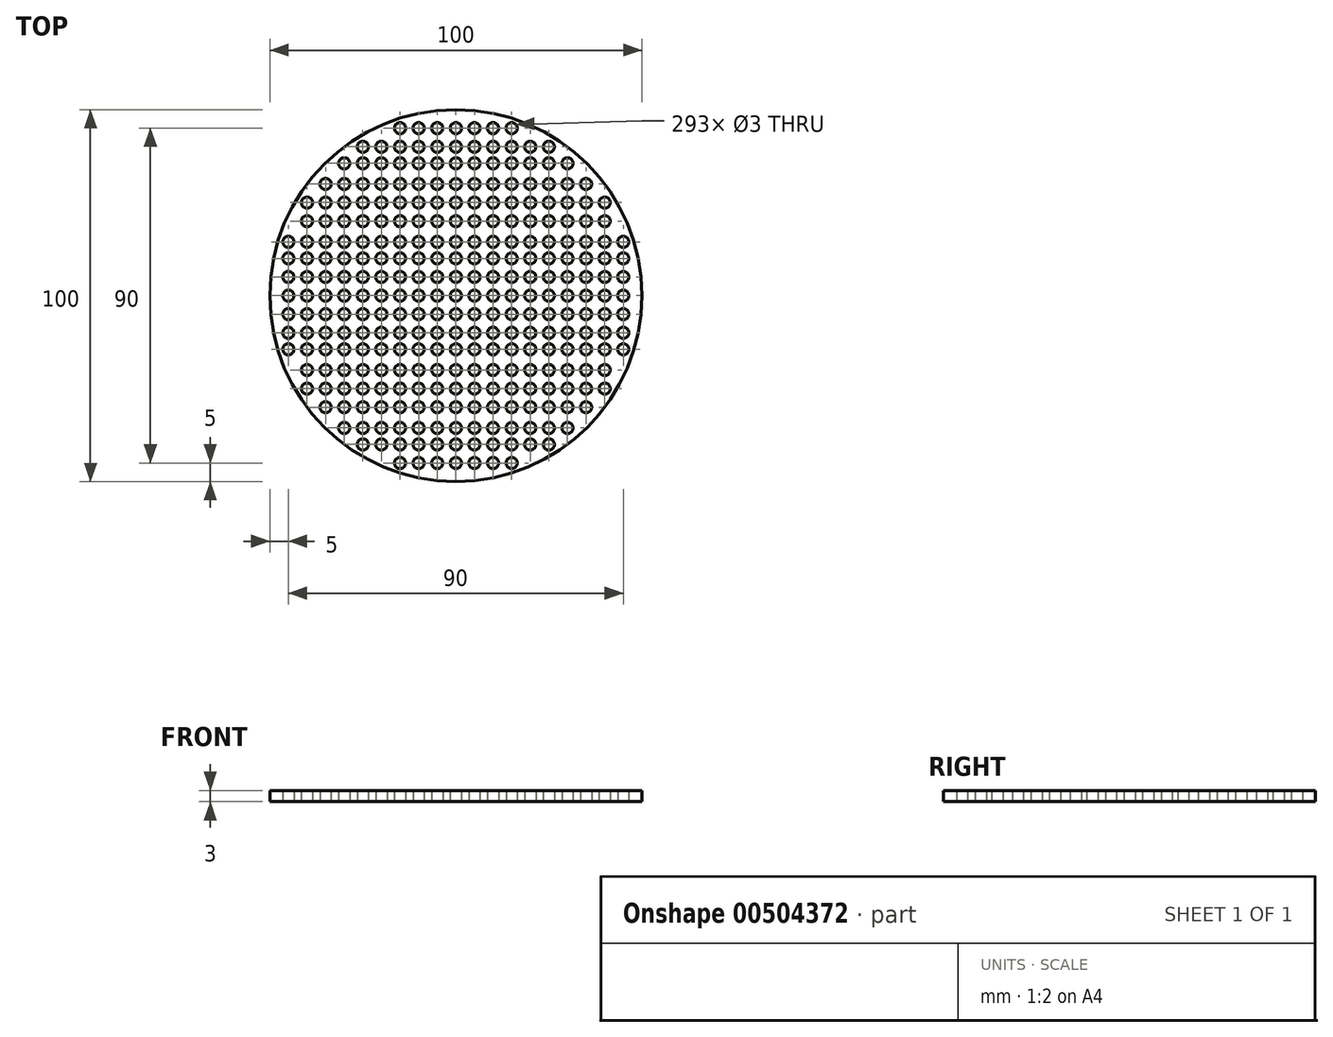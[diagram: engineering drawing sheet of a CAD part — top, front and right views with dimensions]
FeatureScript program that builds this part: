
annotation { "Feature Type Name" : "Feature", "Feature Type Description" : "" }
export const myFeature = defineFeature(function(context is Context, id is Id, definition is map)
    precondition{}
    {
        {
            var Q0;
            Q0=qCreatedBy(makeId("Top.planeOp"),FACE);
            var sketch = newSketch(context, id + "F0", { "sketchPlane" : qUnion([Q0])});
            skLineSegment(sketch, "E0.bottom", {"start": v(0, 0) * mm, "end": v(0, 0) * mm});
            skLineSegment(sketch, "E0.top", {"start": v(0, 0) * mm, "end": v(0, 0) * mm});
            skLineSegment(sketch, "E0.left", {"start": v(0, 0) * mm, "end": v(0, 0) * mm});
            skLineSegment(sketch, "E0.right", {"start": v(0, 0) * mm, "end": v(0, 0) * mm});
            skPoint(sketch, "E0.middle", {"position": v(0, 0) * mm});
            skLineSegment(sketch, "E1.bottom", {"start": v(-5, 5) * mm, "end": v(5, 5) * mm, "construction": true});
            skLineSegment(sketch, "E1.left", {"start": v(-5, 5) * mm, "end": v(-5, -5) * mm, "construction": true});
            skLineSegment(sketch, "E2.bottom", {"start": v(-10, 10) * mm, "end": v(10, 10) * mm, "construction": true});
            skLineSegment(sketch, "E2.left", {"start": v(-10, 10) * mm, "end": v(-10, -10) * mm, "construction": true});
            skLineSegment(sketch, "E2.right", {"start": v(10, 10) * mm, "end": v(10, -10) * mm, "construction": true});
            skLineSegment(sketch, "E3.bottom", {"start": v(15, 14.43) * mm, "end": v(-15, 14.43) * mm, "construction": true});
            skLineSegment(sketch, "E3.left", {"start": v(15, 14.43) * mm, "end": v(15, -14.43) * mm, "construction": true});
            skLineSegment(sketch, "E3.right", {"start": v(-15, 14.43) * mm, "end": v(-15, -14.43) * mm, "construction": true});
            skLineSegment(sketch, "E4.bottom", {"start": v(20, 20) * mm, "end": v(-20, 20) * mm, "construction": true});
            skLineSegment(sketch, "E4.left", {"start": v(20, 20) * mm, "end": v(20, -20) * mm, "construction": true});
            skLineSegment(sketch, "E4.right", {"start": v(-20, 20) * mm, "end": v(-20, -20) * mm, "construction": true});
            skLineSegment(sketch, "E5.bottom", {"start": v(25, 25) * mm, "end": v(-25, 25) * mm, "construction": true});
            skLineSegment(sketch, "E5.left", {"start": v(25, 25) * mm, "end": v(25, -25) * mm, "construction": true});
            skLineSegment(sketch, "E5.right", {"start": v(-25, 25) * mm, "end": v(-25, -25) * mm, "construction": true});
            skCircle(sketch, "E6", {"center": v(0, 0) * mm, "radius": 1.5 * mm});
            skCircle(sketch, "E7", {"center": v(-5, 5) * mm, "radius": 1.5 * mm});
            skCircle(sketch, "E8", {"center": v(-10, 10) * mm, "radius": 1.5 * mm});
            skCircle(sketch, "E9", {"center": v(-15, 14.43) * mm, "radius": 1.5 * mm});
            skCircle(sketch, "E10", {"center": v(-20, 20) * mm, "radius": 1.5 * mm});
            skCircle(sketch, "E11", {"center": v(-25, 25) * mm, "radius": 1.5 * mm});
            skCircle(sketch, "E12", {"center": v(-5, 10) * mm, "radius": 1.5 * mm});
            skCircle(sketch, "E13", {"center": v(-5, 14.43) * mm, "radius": 1.5 * mm});
            skCircle(sketch, "E14", {"center": v(-5, 20) * mm, "radius": 1.5 * mm});
            skCircle(sketch, "E15", {"center": v(-5, 25) * mm, "radius": 1.5 * mm});
            skCircle(sketch, "E16", {"center": v(-10, 14.43) * mm, "radius": 1.5 * mm});
            skCircle(sketch, "E17", {"center": v(-10, 20) * mm, "radius": 1.5 * mm});
            skCircle(sketch, "E18", {"center": v(-10, 25) * mm, "radius": 1.5 * mm});
            skCircle(sketch, "E19", {"center": v(-15, 20) * mm, "radius": 1.5 * mm});
            skCircle(sketch, "E20", {"center": v(-15, 25) * mm, "radius": 1.5 * mm});
            skCircle(sketch, "E21", {"center": v(-20, 25) * mm, "radius": 1.5 * mm});
            skCircle(sketch, "E22", {"center": v(-10, 5) * mm, "radius": 1.5 * mm});
            skCircle(sketch, "E23", {"center": v(-15, 5) * mm, "radius": 1.5 * mm});
            skCircle(sketch, "E24", {"center": v(-20, 5) * mm, "radius": 1.5 * mm});
            skCircle(sketch, "E25", {"center": v(-25, 5) * mm, "radius": 1.5 * mm});
            skCircle(sketch, "E26", {"center": v(-15, 10) * mm, "radius": 1.5 * mm});
            skCircle(sketch, "E27", {"center": v(-20, 10) * mm, "radius": 1.5 * mm});
            skCircle(sketch, "E28", {"center": v(-25, 10) * mm, "radius": 1.5 * mm});
            skCircle(sketch, "E29", {"center": v(-20, 14.43) * mm, "radius": 1.5 * mm});
            skCircle(sketch, "E30", {"center": v(-25, 14.43) * mm, "radius": 1.5 * mm});
            skCircle(sketch, "E31", {"center": v(-25, 20) * mm, "radius": 1.5 * mm});
            skCircle(sketch, "E32", {"center": v(-5, 0) * mm, "radius": 1.5 * mm});
            skCircle(sketch, "E33", {"center": v(-10, 0) * mm, "radius": 1.5 * mm});
            skCircle(sketch, "E34", {"center": v(-15, 0) * mm, "radius": 1.5 * mm});
            skCircle(sketch, "E35", {"center": v(-20, 0) * mm, "radius": 1.5 * mm});
            skCircle(sketch, "E36", {"center": v(-25, 0) * mm, "radius": 1.5 * mm});
            skCircle(sketch, "E37", {"center": v(0, 5) * mm, "radius": 1.5 * mm});
            skCircle(sketch, "E38", {"center": v(0, 10) * mm, "radius": 1.5 * mm});
            skCircle(sketch, "E39", {"center": v(0, 14.43) * mm, "radius": 1.5 * mm});
            skCircle(sketch, "E40", {"center": v(0, 20) * mm, "radius": 1.5 * mm});
            skCircle(sketch, "E41", {"center": v(0, 25) * mm, "radius": 1.5 * mm});
            skCircle(sketch, "E42", {"center": v(0, 0) * mm, "radius": 50 * mm});
            skCircle(sketch, "E43.MirrorC", {"center": v(-15, 30) * mm, "radius": 1.5 * mm});
            skLineSegment(sketch, "E44.MirrorCS", {"start": v(20, 30) * mm, "end": v(-20, 30) * mm, "construction": true});
            skLineSegment(sketch, "E45.MirrorCS", {"start": v(15, 35.57) * mm, "end": v(-15, 35.57) * mm, "construction": true});
            skLineSegment(sketch, "E46.MirrorCS", {"start": v(-10, 40) * mm, "end": v(10, 40) * mm, "construction": true});
            skLineSegment(sketch, "E47.MirrorCS", {"start": v(-5, 45) * mm, "end": v(5, 45) * mm, "construction": true});
            skCircle(sketch, "E48.MirrorC", {"center": v(-10, 30) * mm, "radius": 1.5 * mm});
            skCircle(sketch, "E49.MirrorC", {"center": v(-10, 35.57) * mm, "radius": 1.5 * mm});
            skCircle(sketch, "E50.MirrorC", {"center": v(-5, 30) * mm, "radius": 1.5 * mm});
            skCircle(sketch, "E51.MirrorC", {"center": v(-25, 35.57) * mm, "radius": 1.5 * mm});
            skCircle(sketch, "E52.MirrorC", {"center": v(-20, 40) * mm, "radius": 1.5 * mm});
            skCircle(sketch, "E53.MirrorC", {"center": v(0, 45) * mm, "radius": 1.5 * mm});
            skCircle(sketch, "E54.MirrorC", {"center": v(-25, 40) * mm, "radius": 1.5 * mm});
            skCircle(sketch, "E55.MirrorC", {"center": v(-5, 40) * mm, "radius": 1.5 * mm});
            skCircle(sketch, "E56.MirrorC", {"center": v(0, 40) * mm, "radius": 1.5 * mm});
            skCircle(sketch, "E57.MirrorC", {"center": v(-10, 45) * mm, "radius": 1.5 * mm});
            skCircle(sketch, "E58.MirrorC", {"center": v(-25, 30) * mm, "radius": 1.5 * mm});
            skCircle(sketch, "E59.MirrorC", {"center": v(-15, 40) * mm, "radius": 1.5 * mm});
            skCircle(sketch, "E60.MirrorC", {"center": v(-20, 35.57) * mm, "radius": 1.5 * mm});
            skCircle(sketch, "E61.MirrorC", {"center": v(-5, 45) * mm, "radius": 1.5 * mm});
            skCircle(sketch, "E62.MirrorC", {"center": v(-20, 30) * mm, "radius": 1.5 * mm});
            skCircle(sketch, "E63.MirrorC", {"center": v(0, 30) * mm, "radius": 1.5 * mm});
            skCircle(sketch, "E64.MirrorC", {"center": v(-10, 40) * mm, "radius": 1.5 * mm});
            skCircle(sketch, "E65.MirrorC", {"center": v(-15, 45) * mm, "radius": 1.5 * mm});
            skCircle(sketch, "E66.MirrorC", {"center": v(-15, 35.57) * mm, "radius": 1.5 * mm});
            skCircle(sketch, "E67.MirrorC", {"center": v(-5, 35.57) * mm, "radius": 1.5 * mm});
            skCircle(sketch, "E68.MirrorC", {"center": v(0, 35.57) * mm, "radius": 1.5 * mm});
            skCircle(sketch, "E69.MirrorC", {"center": v(-35, 25) * mm, "radius": 1.5 * mm});
            skCircle(sketch, "E70.MirrorC", {"center": v(-35, 20) * mm, "radius": 1.5 * mm});
            skCircle(sketch, "E71.MirrorC", {"center": v(-40, 25) * mm, "radius": 1.5 * mm});
            skCircle(sketch, "E72.MirrorC", {"center": v(-30, 25) * mm, "radius": 1.5 * mm});
            skCircle(sketch, "E73.MirrorC", {"center": v(-40, 5) * mm, "radius": 1.5 * mm});
            skCircle(sketch, "E74.MirrorC", {"center": v(-35, 30) * mm, "radius": 1.5 * mm});
            skCircle(sketch, "E75.MirrorC", {"center": v(-45, 5) * mm, "radius": 1.5 * mm});
            skCircle(sketch, "E76.MirrorC", {"center": v(-35, 5) * mm, "radius": 1.5 * mm});
            skCircle(sketch, "E77.MirrorC", {"center": v(-40, 10) * mm, "radius": 1.5 * mm});
            skCircle(sketch, "E78.MirrorC", {"center": v(-30, 5) * mm, "radius": 1.5 * mm});
            skCircle(sketch, "E79.MirrorC", {"center": v(-30, 35.57) * mm, "radius": 1.5 * mm});
            skCircle(sketch, "E80.MirrorC", {"center": v(-35, 14.43) * mm, "radius": 1.5 * mm});
            skCircle(sketch, "E81.MirrorC", {"center": v(-45, 10) * mm, "radius": 1.5 * mm});
            skCircle(sketch, "E82.MirrorC", {"center": v(-40, 20) * mm, "radius": 1.5 * mm});
            skCircle(sketch, "E83.MirrorC", {"center": v(-30, 20) * mm, "radius": 1.5 * mm});
            skCircle(sketch, "E84.MirrorC", {"center": v(-45, 14.43) * mm, "radius": 1.5 * mm});
            skCircle(sketch, "E85.MirrorC", {"center": v(-30, 14.43) * mm, "radius": 1.5 * mm});
            skCircle(sketch, "E86.MirrorC", {"center": v(-30, 10) * mm, "radius": 1.5 * mm});
            skCircle(sketch, "E87.MirrorC", {"center": v(-40, 14.43) * mm, "radius": 1.5 * mm});
            skCircle(sketch, "E88.MirrorC", {"center": v(-30, 30) * mm, "radius": 1.5 * mm});
            skCircle(sketch, "E89.MirrorC", {"center": v(-35, 10) * mm, "radius": 1.5 * mm});
            skCircle(sketch, "E90.MirrorC", {"center": v(-40, 0) * mm, "radius": 1.5 * mm});
            skCircle(sketch, "E91.MirrorC", {"center": v(-45, 0) * mm, "radius": 1.5 * mm});
            skCircle(sketch, "E92.MirrorC", {"center": v(-35, 0) * mm, "radius": 1.5 * mm});
            skCircle(sketch, "E93.MirrorC", {"center": v(-30, 0) * mm, "radius": 1.5 * mm});
            skLineSegment(sketch, "E94.MirrorCS", {"start": v(5, 5) * mm, "end": v(-5, 5) * mm, "construction": true});
            skCircle(sketch, "E95.MirrorC", {"center": v(5, 5) * mm, "radius": 1.5 * mm});
            skCircle(sketch, "E96.MirrorC", {"center": v(40, 5) * mm, "radius": 1.5 * mm});
            skCircle(sketch, "E97.MirrorC", {"center": v(10, 10) * mm, "radius": 1.5 * mm});
            skCircle(sketch, "E98.MirrorC", {"center": v(35, 5) * mm, "radius": 1.5 * mm});
            skCircle(sketch, "E99.MirrorC", {"center": v(25, 25) * mm, "radius": 1.5 * mm});
            skCircle(sketch, "E100.MirrorC", {"center": v(10, 40) * mm, "radius": 1.5 * mm});
            skCircle(sketch, "E101.MirrorC", {"center": v(5, 45) * mm, "radius": 1.5 * mm});
            skCircle(sketch, "E102.MirrorC", {"center": v(20, 30) * mm, "radius": 1.5 * mm});
            skLineSegment(sketch, "E103.MirrorCS", {"start": v(5, 45) * mm, "end": v(-5, 45) * mm, "construction": true});
            skCircle(sketch, "E104.MirrorC", {"center": v(25, 35.57) * mm, "radius": 1.5 * mm});
            skCircle(sketch, "E105.MirrorC", {"center": v(5, 40) * mm, "radius": 1.5 * mm});
            skCircle(sketch, "E106.MirrorC", {"center": v(25, 10) * mm, "radius": 1.5 * mm});
            skCircle(sketch, "E107.MirrorC", {"center": v(5, 35.57) * mm, "radius": 1.5 * mm});
            skCircle(sketch, "E108.MirrorC", {"center": v(35, 30) * mm, "radius": 1.5 * mm});
            skCircle(sketch, "E109.MirrorC", {"center": v(25, 30) * mm, "radius": 1.5 * mm});
            skCircle(sketch, "E110.MirrorC", {"center": v(5, 25) * mm, "radius": 1.5 * mm});
            skCircle(sketch, "E111.MirrorC", {"center": v(45, 5) * mm, "radius": 1.5 * mm});
            skCircle(sketch, "E112.MirrorC", {"center": v(20, 40) * mm, "radius": 1.5 * mm});
            skCircle(sketch, "E113.MirrorC", {"center": v(25, 40) * mm, "radius": 1.5 * mm});
            skCircle(sketch, "E114.MirrorC", {"center": v(10, 5) * mm, "radius": 1.5 * mm});
            skCircle(sketch, "E115.MirrorC", {"center": v(30, 5) * mm, "radius": 1.5 * mm});
            skCircle(sketch, "E116.MirrorC", {"center": v(35, 0) * mm, "radius": 1.5 * mm});
            skCircle(sketch, "E117.MirrorC", {"center": v(5, 30) * mm, "radius": 1.5 * mm});
            skCircle(sketch, "E118.MirrorC", {"center": v(35, 10) * mm, "radius": 1.5 * mm});
            skCircle(sketch, "E119.MirrorC", {"center": v(40, 25) * mm, "radius": 1.5 * mm});
            skCircle(sketch, "E120.MirrorC", {"center": v(10, 25) * mm, "radius": 1.5 * mm});
            skCircle(sketch, "E121.MirrorC", {"center": v(20, 10) * mm, "radius": 1.5 * mm});
            skCircle(sketch, "E122.MirrorC", {"center": v(40, 10) * mm, "radius": 1.5 * mm});
            skCircle(sketch, "E123.MirrorC", {"center": v(20, 35.57) * mm, "radius": 1.5 * mm});
            skCircle(sketch, "E124.MirrorC", {"center": v(5, 10) * mm, "radius": 1.5 * mm});
            skCircle(sketch, "E125.MirrorC", {"center": v(20, 5) * mm, "radius": 1.5 * mm});
            skCircle(sketch, "E126.MirrorC", {"center": v(10, 30) * mm, "radius": 1.5 * mm});
            skCircle(sketch, "E127.MirrorC", {"center": v(25, 5) * mm, "radius": 1.5 * mm});
            skCircle(sketch, "E128.MirrorC", {"center": v(10, 35.57) * mm, "radius": 1.5 * mm});
            skCircle(sketch, "E129.MirrorC", {"center": v(20, 25) * mm, "radius": 1.5 * mm});
            skCircle(sketch, "E130.MirrorC", {"center": v(10, 45) * mm, "radius": 1.5 * mm});
            skCircle(sketch, "E131.MirrorC", {"center": v(35, 25) * mm, "radius": 1.5 * mm});
            skCircle(sketch, "E132.MirrorC", {"center": v(15, 30) * mm, "radius": 1.5 * mm});
            skCircle(sketch, "E133.MirrorC", {"center": v(30, 20) * mm, "radius": 1.5 * mm});
            skCircle(sketch, "E134.MirrorC", {"center": v(40, 20) * mm, "radius": 1.5 * mm});
            skLineSegment(sketch, "E135.MirrorCS", {"start": v(10, 40) * mm, "end": v(-10, 40) * mm, "construction": true});
            skLineSegment(sketch, "E136.MirrorCS", {"start": v(5, 5) * mm, "end": v(5, -5) * mm, "construction": true});
            skLineSegment(sketch, "E137.MirrorCS", {"start": v(-15, 14.43) * mm, "end": v(15, 14.43) * mm, "construction": true});
            skLineSegment(sketch, "E138.MirrorCS", {"start": v(-20, 20) * mm, "end": v(20, 20) * mm, "construction": true});
            skLineSegment(sketch, "E139.MirrorCS", {"start": v(-25, 25) * mm, "end": v(25, 25) * mm, "construction": true});
            skCircle(sketch, "E140.MirrorC", {"center": v(15, 20) * mm, "radius": 1.5 * mm});
            skCircle(sketch, "E141.MirrorC", {"center": v(20, 0) * mm, "radius": 1.5 * mm});
            skCircle(sketch, "E142.MirrorC", {"center": v(30, 10) * mm, "radius": 1.5 * mm});
            skLineSegment(sketch, "E143.MirrorCS", {"start": v(-15, 35.57) * mm, "end": v(15, 35.57) * mm, "construction": true});
            skCircle(sketch, "E144.MirrorC", {"center": v(20, 14.43) * mm, "radius": 1.5 * mm});
            skLineSegment(sketch, "E145.MirrorCS", {"start": v(-20, 30) * mm, "end": v(20, 30) * mm, "construction": true});
            skCircle(sketch, "E146.MirrorC", {"center": v(15, 5) * mm, "radius": 1.5 * mm});
            skCircle(sketch, "E147.MirrorC", {"center": v(30, 30) * mm, "radius": 1.5 * mm});
            skCircle(sketch, "E148.MirrorC", {"center": v(45, 0) * mm, "radius": 1.5 * mm});
            skCircle(sketch, "E149.MirrorC", {"center": v(45, 14.43) * mm, "radius": 1.5 * mm});
            skCircle(sketch, "E150.MirrorC", {"center": v(15, 25) * mm, "radius": 1.5 * mm});
            skCircle(sketch, "E151.MirrorC", {"center": v(5, 14.43) * mm, "radius": 1.5 * mm});
            skCircle(sketch, "E152.MirrorC", {"center": v(35, 20) * mm, "radius": 1.5 * mm});
            skCircle(sketch, "E153.MirrorC", {"center": v(30, 25) * mm, "radius": 1.5 * mm});
            skCircle(sketch, "E154.MirrorC", {"center": v(10, 14.43) * mm, "radius": 1.5 * mm});
            skCircle(sketch, "E155.MirrorC", {"center": v(35, 14.43) * mm, "radius": 1.5 * mm});
            skCircle(sketch, "E156.MirrorC", {"center": v(5, 20) * mm, "radius": 1.5 * mm});
            skCircle(sketch, "E157.MirrorC", {"center": v(25, 14.43) * mm, "radius": 1.5 * mm});
            skCircle(sketch, "E158.MirrorC", {"center": v(10, 0) * mm, "radius": 1.5 * mm});
            skLineSegment(sketch, "E159.MirrorCS", {"start": v(10, 10) * mm, "end": v(-10, 10) * mm, "construction": true});
            skCircle(sketch, "E160.MirrorC", {"center": v(10, 20) * mm, "radius": 1.5 * mm});
            skCircle(sketch, "E161.MirrorC", {"center": v(15, 35.57) * mm, "radius": 1.5 * mm});
            skCircle(sketch, "E162.MirrorC", {"center": v(15, 10) * mm, "radius": 1.5 * mm});
            skCircle(sketch, "E163.MirrorC", {"center": v(15, 45) * mm, "radius": 1.5 * mm});
            skCircle(sketch, "E164.MirrorC", {"center": v(20, 20) * mm, "radius": 1.5 * mm});
            skCircle(sketch, "E165.MirrorC", {"center": v(30, 0) * mm, "radius": 1.5 * mm});
            skCircle(sketch, "E166.MirrorC", {"center": v(15, 0) * mm, "radius": 1.5 * mm});
            skCircle(sketch, "E167.MirrorC", {"center": v(30, 35.57) * mm, "radius": 1.5 * mm});
            skCircle(sketch, "E168.MirrorC", {"center": v(15, 40) * mm, "radius": 1.5 * mm});
            skCircle(sketch, "E169.MirrorC", {"center": v(40, 14.43) * mm, "radius": 1.5 * mm});
            skCircle(sketch, "E170.MirrorC", {"center": v(40, 0) * mm, "radius": 1.5 * mm});
            skCircle(sketch, "E171.MirrorC", {"center": v(25, 0) * mm, "radius": 1.5 * mm});
            skCircle(sketch, "E172.MirrorC", {"center": v(45, 10) * mm, "radius": 1.5 * mm});
            skCircle(sketch, "E173.MirrorC", {"center": v(30, 14.43) * mm, "radius": 1.5 * mm});
            skCircle(sketch, "E174.MirrorC", {"center": v(15, 14.43) * mm, "radius": 1.5 * mm});
            skCircle(sketch, "E175.MirrorC", {"center": v(5, 0) * mm, "radius": 1.5 * mm});
            skCircle(sketch, "E176.MirrorC", {"center": v(25, 20) * mm, "radius": 1.5 * mm});
            skCircle(sketch, "E177.MirrorC", {"center": v(20, -20) * mm, "radius": 1.5 * mm});
            skCircle(sketch, "E178.MirrorC", {"center": v(25, -25) * mm, "radius": 1.5 * mm});
            skCircle(sketch, "E179.MirrorC", {"center": v(-25, -25) * mm, "radius": 1.5 * mm});
            skCircle(sketch, "E180.MirrorC", {"center": v(5, -5) * mm, "radius": 1.5 * mm});
            skCircle(sketch, "E181.MirrorC", {"center": v(-10, -10) * mm, "radius": 1.5 * mm});
            skCircle(sketch, "E182.MirrorC", {"center": v(-30, -5) * mm, "radius": 1.5 * mm});
            skCircle(sketch, "E183.MirrorC", {"center": v(20, -30) * mm, "radius": 1.5 * mm});
            skCircle(sketch, "E184.MirrorC", {"center": v(35, -5) * mm, "radius": 1.5 * mm});
            skCircle(sketch, "E185.MirrorC", {"center": v(-10, -40) * mm, "radius": 1.5 * mm});
            skCircle(sketch, "E186.MirrorC", {"center": v(5, -45) * mm, "radius": 1.5 * mm});
            skCircle(sketch, "E187.MirrorC", {"center": v(-40, -5) * mm, "radius": 1.5 * mm});
            skCircle(sketch, "E188.MirrorC", {"center": v(-45, -5) * mm, "radius": 1.5 * mm});
            skLineSegment(sketch, "E189.MirrorCS", {"start": v(5, -45) * mm, "end": v(-5, -45) * mm, "construction": true});
            skCircle(sketch, "E190.MirrorC", {"center": v(40, -25) * mm, "radius": 1.5 * mm});
            skCircle(sketch, "E191.MirrorC", {"center": v(-40, -10) * mm, "radius": 1.5 * mm});
            skCircle(sketch, "E192.MirrorC", {"center": v(15, -10) * mm, "radius": 1.5 * mm});
            skCircle(sketch, "E193.MirrorC", {"center": v(40, -5) * mm, "radius": 1.5 * mm});
            skCircle(sketch, "E194.MirrorC", {"center": v(35, -10) * mm, "radius": 1.5 * mm});
            skCircle(sketch, "E195.MirrorC", {"center": v(-25, -10) * mm, "radius": 1.5 * mm});
            skCircle(sketch, "E196.MirrorC", {"center": v(-35, -5) * mm, "radius": 1.5 * mm});
            skCircle(sketch, "E197.MirrorC", {"center": v(5, -30) * mm, "radius": 1.5 * mm});
            skCircle(sketch, "E198.MirrorC", {"center": v(-15, -30) * mm, "radius": 1.5 * mm});
            skCircle(sketch, "E199.MirrorC", {"center": v(20, -35.57) * mm, "radius": 1.5 * mm});
            skCircle(sketch, "E200.MirrorC", {"center": v(-15, -40) * mm, "radius": 1.5 * mm});
            skCircle(sketch, "E201.MirrorC", {"center": v(35, -20) * mm, "radius": 1.5 * mm});
            skCircle(sketch, "E202.MirrorC", {"center": v(-15, -45) * mm, "radius": 1.5 * mm});
            skCircle(sketch, "E203.MirrorC", {"center": v(-45, -10) * mm, "radius": 1.5 * mm});
            skCircle(sketch, "E204.MirrorC", {"center": v(-10, -20) * mm, "radius": 1.5 * mm});
            skLineSegment(sketch, "E205.MirrorCS", {"start": v(-20, -30) * mm, "end": v(20, -30) * mm, "construction": true});
            skLineSegment(sketch, "E206.MirrorCS", {"start": v(-10, -40) * mm, "end": v(10, -40) * mm, "construction": true});
            skCircle(sketch, "E207.MirrorC", {"center": v(35, -30) * mm, "radius": 1.5 * mm});
            skCircle(sketch, "E208.MirrorC", {"center": v(30, -5) * mm, "radius": 1.5 * mm});
            skCircle(sketch, "E209.MirrorC", {"center": v(-15, -5) * mm, "radius": 1.5 * mm});
            skCircle(sketch, "E210.MirrorC", {"center": v(-15, -20) * mm, "radius": 1.5 * mm});
            skCircle(sketch, "E211.MirrorC", {"center": v(-10, -30) * mm, "radius": 1.5 * mm});
            skCircle(sketch, "E212.MirrorC", {"center": v(5, -10) * mm, "radius": 1.5 * mm});
            skCircle(sketch, "E213.MirrorC", {"center": v(20, -5) * mm, "radius": 1.5 * mm});
            skCircle(sketch, "E214.MirrorC", {"center": v(-30, -10) * mm, "radius": 1.5 * mm});
            skCircle(sketch, "E215.MirrorC", {"center": v(20, -40) * mm, "radius": 1.5 * mm});
            skCircle(sketch, "E216.MirrorC", {"center": v(-10, -5) * mm, "radius": 1.5 * mm});
            skCircle(sketch, "E217.MirrorC", {"center": v(0, -10) * mm, "radius": 1.5 * mm});
            skLineSegment(sketch, "E218.MirrorCS", {"start": v(5, -5) * mm, "end": v(-5, -5) * mm, "construction": true});
            skLineSegment(sketch, "E219.MirrorCS", {"start": v(-20, -20) * mm, "end": v(20, -20) * mm, "construction": true});
            skCircle(sketch, "E220.MirrorC", {"center": v(-10, -25) * mm, "radius": 1.5 * mm});
            skCircle(sketch, "E221.MirrorC", {"center": v(0, -40) * mm, "radius": 1.5 * mm});
            skLineSegment(sketch, "E222.MirrorCS", {"start": v(-25, -25) * mm, "end": v(25, -25) * mm, "construction": true});
            skCircle(sketch, "E223.MirrorC", {"center": v(-25, -40) * mm, "radius": 1.5 * mm});
            skCircle(sketch, "E224.MirrorC", {"center": v(-15, -10) * mm, "radius": 1.5 * mm});
            skCircle(sketch, "E225.MirrorC", {"center": v(5, -25) * mm, "radius": 1.5 * mm});
            skCircle(sketch, "E226.MirrorC", {"center": v(-30, -25) * mm, "radius": 1.5 * mm});
            skCircle(sketch, "E227.MirrorC", {"center": v(-30, -30) * mm, "radius": 1.5 * mm});
            skCircle(sketch, "E228.MirrorC", {"center": v(25, -40) * mm, "radius": 1.5 * mm});
            skLineSegment(sketch, "E229.MirrorCS", {"start": v(-15, -14.43) * mm, "end": v(15, -14.43) * mm, "construction": true});
            skCircle(sketch, "E230.MirrorC", {"center": v(40, -10) * mm, "radius": 1.5 * mm});
            skCircle(sketch, "E231.MirrorC", {"center": v(-40, -25) * mm, "radius": 1.5 * mm});
            skCircle(sketch, "E232.MirrorC", {"center": v(45, -5) * mm, "radius": 1.5 * mm});
            skCircle(sketch, "E233.MirrorC", {"center": v(-30, -20) * mm, "radius": 1.5 * mm});
            skCircle(sketch, "E234.MirrorC", {"center": v(5, -20) * mm, "radius": 1.5 * mm});
            skLineSegment(sketch, "E235.MirrorCS", {"start": v(-15, -35.57) * mm, "end": v(15, -35.57) * mm, "construction": true});
            skCircle(sketch, "E236.MirrorC", {"center": v(20, -14.43) * mm, "radius": 1.5 * mm});
            skCircle(sketch, "E237.MirrorC", {"center": v(15, -40) * mm, "radius": 1.5 * mm});
            skCircle(sketch, "E238.MirrorC", {"center": v(-15, -25) * mm, "radius": 1.5 * mm});
            skCircle(sketch, "E239.MirrorC", {"center": v(0, -25) * mm, "radius": 1.5 * mm});
            skCircle(sketch, "E240.MirrorC", {"center": v(-10, -45) * mm, "radius": 1.5 * mm});
            skCircle(sketch, "E241.MirrorC", {"center": v(35, -25) * mm, "radius": 1.5 * mm});
            skCircle(sketch, "E242.MirrorC", {"center": v(-25, -30) * mm, "radius": 1.5 * mm});
            skCircle(sketch, "E243.MirrorC", {"center": v(20, -25) * mm, "radius": 1.5 * mm});
            skLineSegment(sketch, "E244.MirrorCS", {"start": v(10, -10) * mm, "end": v(-10, -10) * mm, "construction": true});
            skCircle(sketch, "E245.MirrorC", {"center": v(20, -10) * mm, "radius": 1.5 * mm});
            skCircle(sketch, "E246.MirrorC", {"center": v(25, -10) * mm, "radius": 1.5 * mm});
            skCircle(sketch, "E247.MirrorC", {"center": v(5, -40) * mm, "radius": 1.5 * mm});
            skCircle(sketch, "E248.MirrorC", {"center": v(-25, -5) * mm, "radius": 1.5 * mm});
            skCircle(sketch, "E249.MirrorC", {"center": v(15, -25) * mm, "radius": 1.5 * mm});
            skCircle(sketch, "E250.MirrorC", {"center": v(15, -45) * mm, "radius": 1.5 * mm});
            skCircle(sketch, "E251.MirrorC", {"center": v(25, -20) * mm, "radius": 1.5 * mm});
            skCircle(sketch, "E252.MirrorC", {"center": v(-20, -14.43) * mm, "radius": 1.5 * mm});
            skLineSegment(sketch, "E253.MirrorCS", {"start": v(15, -35.57) * mm, "end": v(-15, -35.57) * mm, "construction": true});
            skCircle(sketch, "E254.MirrorC", {"center": v(-5, -45) * mm, "radius": 1.5 * mm});
            skCircle(sketch, "E255.MirrorC", {"center": v(-5, -14.43) * mm, "radius": 1.5 * mm});
            skCircle(sketch, "E256.MirrorC", {"center": v(30, -30) * mm, "radius": 1.5 * mm});
            skCircle(sketch, "E257.MirrorC", {"center": v(40, -20) * mm, "radius": 1.5 * mm});
            skLineSegment(sketch, "E258.MirrorCS", {"start": v(20, -30) * mm, "end": v(-20, -30) * mm, "construction": true});
            skCircle(sketch, "E259.MirrorC", {"center": v(-20, -35.57) * mm, "radius": 1.5 * mm});
            skCircle(sketch, "E260.MirrorC", {"center": v(-5, -10) * mm, "radius": 1.5 * mm});
            skCircle(sketch, "E261.MirrorC", {"center": v(15, -5) * mm, "radius": 1.5 * mm});
            skCircle(sketch, "E262.MirrorC", {"center": v(15, -35.57) * mm, "radius": 1.5 * mm});
            skCircle(sketch, "E263.MirrorC", {"center": v(15, -14.43) * mm, "radius": 1.5 * mm});
            skCircle(sketch, "E264.MirrorC", {"center": v(30, -20) * mm, "radius": 1.5 * mm});
            skCircle(sketch, "E265.MirrorC", {"center": v(-20, -10) * mm, "radius": 1.5 * mm});
            skCircle(sketch, "E266.MirrorC", {"center": v(5, -35.57) * mm, "radius": 1.5 * mm});
            skCircle(sketch, "E267.MirrorC", {"center": v(10, -20) * mm, "radius": 1.5 * mm});
            skCircle(sketch, "E268.MirrorC", {"center": v(30, -14.43) * mm, "radius": 1.5 * mm});
            skCircle(sketch, "E269.MirrorC", {"center": v(-5, -20) * mm, "radius": 1.5 * mm});
            skCircle(sketch, "E270.MirrorC", {"center": v(-20, -30) * mm, "radius": 1.5 * mm});
            skCircle(sketch, "E271.MirrorC", {"center": v(-25, -14.43) * mm, "radius": 1.5 * mm});
            skLineSegment(sketch, "E272.MirrorCS", {"start": v(10, -40) * mm, "end": v(-10, -40) * mm, "construction": true});
            skCircle(sketch, "E273.MirrorC", {"center": v(10, -25) * mm, "radius": 1.5 * mm});
            skCircle(sketch, "E274.MirrorC", {"center": v(25, -35.57) * mm, "radius": 1.5 * mm});
            skCircle(sketch, "E275.MirrorC", {"center": v(-35, -20) * mm, "radius": 1.5 * mm});
            skCircle(sketch, "E276.MirrorC", {"center": v(10, -40) * mm, "radius": 1.5 * mm});
            skCircle(sketch, "E277.MirrorC", {"center": v(30, -10) * mm, "radius": 1.5 * mm});
            skCircle(sketch, "E278.MirrorC", {"center": v(25, -30) * mm, "radius": 1.5 * mm});
            skCircle(sketch, "E279.MirrorC", {"center": v(30, -35.57) * mm, "radius": 1.5 * mm});
            skCircle(sketch, "E280.MirrorC", {"center": v(-45, -14.43) * mm, "radius": 1.5 * mm});
            skCircle(sketch, "E281.MirrorC", {"center": v(15, -30) * mm, "radius": 1.5 * mm});
            skCircle(sketch, "E282.MirrorC", {"center": v(-5, -40) * mm, "radius": 1.5 * mm});
            skCircle(sketch, "E283.MirrorC", {"center": v(10, -35.57) * mm, "radius": 1.5 * mm});
            skLineSegment(sketch, "E284.MirrorCS", {"start": v(20, -20) * mm, "end": v(-20, -20) * mm, "construction": true});
            skCircle(sketch, "E285.MirrorC", {"center": v(10, -45) * mm, "radius": 1.5 * mm});
            skLineSegment(sketch, "E286.MirrorCS", {"start": v(15, -14.43) * mm, "end": v(-15, -14.43) * mm, "construction": true});
            skCircle(sketch, "E287.MirrorC", {"center": v(-15, -35.57) * mm, "radius": 1.5 * mm});
            skCircle(sketch, "E288.MirrorC", {"center": v(-10, -14.43) * mm, "radius": 1.5 * mm});
            skCircle(sketch, "E289.MirrorC", {"center": v(45, -14.43) * mm, "radius": 1.5 * mm});
            skCircle(sketch, "E290.MirrorC", {"center": v(-30, -35.57) * mm, "radius": 1.5 * mm});
            skCircle(sketch, "E291.MirrorC", {"center": v(-20, -5) * mm, "radius": 1.5 * mm});
            skCircle(sketch, "E292.MirrorC", {"center": v(0, -20) * mm, "radius": 1.5 * mm});
            skCircle(sketch, "E293.MirrorC", {"center": v(0, -30) * mm, "radius": 1.5 * mm});
            skCircle(sketch, "E294.MirrorC", {"center": v(-40, -20) * mm, "radius": 1.5 * mm});
            skCircle(sketch, "E295.MirrorC", {"center": v(35, -14.43) * mm, "radius": 1.5 * mm});
            skCircle(sketch, "E296.MirrorC", {"center": v(0, -35.57) * mm, "radius": 1.5 * mm});
            skLineSegment(sketch, "E297.MirrorCS", {"start": v(-5, -45) * mm, "end": v(5, -45) * mm, "construction": true});
            skCircle(sketch, "E298.MirrorC", {"center": v(-25, -20) * mm, "radius": 1.5 * mm});
            skCircle(sketch, "E299.MirrorC", {"center": v(15, -20) * mm, "radius": 1.5 * mm});
            skCircle(sketch, "E300.MirrorC", {"center": v(45, -10) * mm, "radius": 1.5 * mm});
            skLineSegment(sketch, "E301.MirrorCS", {"start": v(-10, -10) * mm, "end": v(10, -10) * mm, "construction": true});
            skLineSegment(sketch, "E302.MirrorCS", {"start": v(25, -25) * mm, "end": v(-25, -25) * mm, "construction": true});
            skCircle(sketch, "E303.MirrorC", {"center": v(-5, -5) * mm, "radius": 1.5 * mm});
            skCircle(sketch, "E304.MirrorC", {"center": v(30, -25) * mm, "radius": 1.5 * mm});
            skCircle(sketch, "E305.MirrorC", {"center": v(25, -14.43) * mm, "radius": 1.5 * mm});
            skCircle(sketch, "E306.MirrorC", {"center": v(40, -14.43) * mm, "radius": 1.5 * mm});
            skCircle(sketch, "E307.MirrorC", {"center": v(10, -10) * mm, "radius": 1.5 * mm});
            skCircle(sketch, "E308.MirrorC", {"center": v(-30, -14.43) * mm, "radius": 1.5 * mm});
            skCircle(sketch, "E309.MirrorC", {"center": v(5, -14.43) * mm, "radius": 1.5 * mm});
            skCircle(sketch, "E310.MirrorC", {"center": v(0, -14.43) * mm, "radius": 1.5 * mm});
            skCircle(sketch, "E311.MirrorC", {"center": v(10, -14.43) * mm, "radius": 1.5 * mm});
            skCircle(sketch, "E312.MirrorC", {"center": v(-5, -35.57) * mm, "radius": 1.5 * mm});
            skCircle(sketch, "E313.MirrorC", {"center": v(-35, -14.43) * mm, "radius": 1.5 * mm});
            skLineSegment(sketch, "E314.MirrorCS", {"start": v(-5, -5) * mm, "end": v(5, -5) * mm, "construction": true});
            skCircle(sketch, "E315.MirrorC", {"center": v(-25, -35.57) * mm, "radius": 1.5 * mm});
            skCircle(sketch, "E316.MirrorC", {"center": v(25, -5) * mm, "radius": 1.5 * mm});
            skCircle(sketch, "E317.MirrorC", {"center": v(-5, -25) * mm, "radius": 1.5 * mm});
            skCircle(sketch, "E318.MirrorC", {"center": v(-20, -25) * mm, "radius": 1.5 * mm});
            skCircle(sketch, "E319.MirrorC", {"center": v(0, -5) * mm, "radius": 1.5 * mm});
            skCircle(sketch, "E320.MirrorC", {"center": v(-10, -35.57) * mm, "radius": 1.5 * mm});
            skCircle(sketch, "E321.MirrorC", {"center": v(0, -45) * mm, "radius": 1.5 * mm});
            skCircle(sketch, "E322.MirrorC", {"center": v(-35, -25) * mm, "radius": 1.5 * mm});
            skCircle(sketch, "E323.MirrorC", {"center": v(-15, -14.43) * mm, "radius": 1.5 * mm});
            skCircle(sketch, "E324.MirrorC", {"center": v(-20, -40) * mm, "radius": 1.5 * mm});
            skCircle(sketch, "E325.MirrorC", {"center": v(-35, -30) * mm, "radius": 1.5 * mm});
            skCircle(sketch, "E326.MirrorC", {"center": v(10, -5) * mm, "radius": 1.5 * mm});
            skCircle(sketch, "E327.MirrorC", {"center": v(-20, -20) * mm, "radius": 1.5 * mm});
            skCircle(sketch, "E328.MirrorC", {"center": v(10, -30) * mm, "radius": 1.5 * mm});
            skCircle(sketch, "E329.MirrorC", {"center": v(-35, -10) * mm, "radius": 1.5 * mm});
            skCircle(sketch, "E330.MirrorC", {"center": v(-40, -14.43) * mm, "radius": 1.5 * mm});
            skCircle(sketch, "E331.MirrorC", {"center": v(-5, -30) * mm, "radius": 1.5 * mm});
            skSolve(sketch);
        }
        {
            var Q0;
            Q0 = qSketchRegion(id + "F0", true);
            extrude(context, id + "F1", {"entities" : qUnion([Q0]), "depth" : 3 * mm, "offsetDistance" : 25 * mm});
        }
    });
